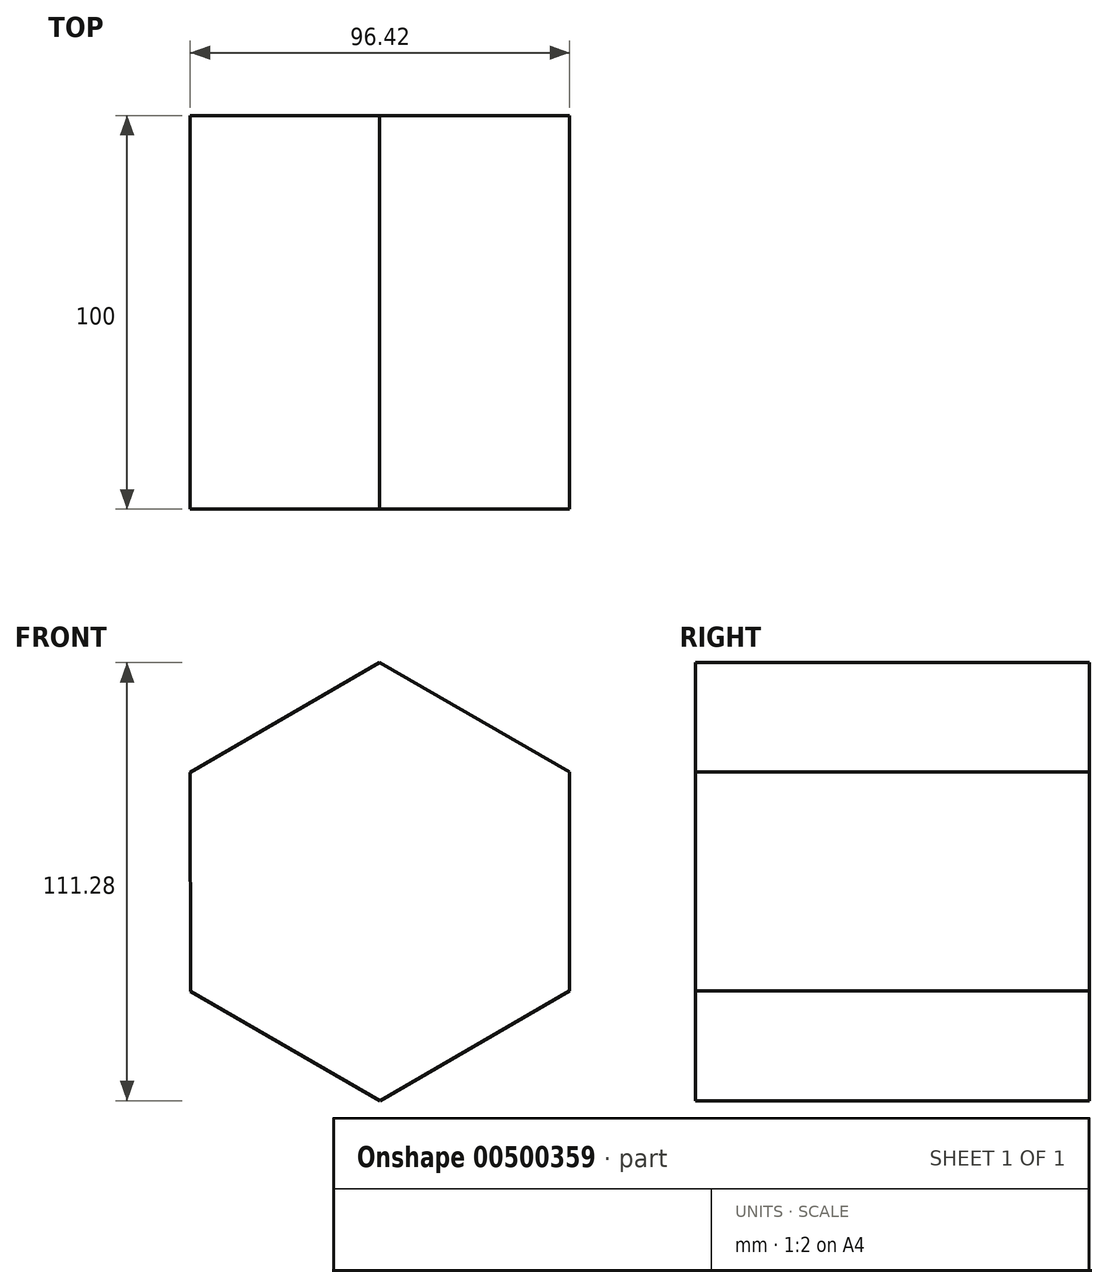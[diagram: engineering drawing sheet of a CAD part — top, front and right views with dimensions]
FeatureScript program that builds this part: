
annotation { "Feature Type Name" : "Feature", "Feature Type Description" : "" }
export const myFeature = defineFeature(function(context is Context, id is Id, definition is map)
    precondition{}
    {
        {
            var Q0;
            Q0=qCreatedBy(makeId("Front.planeOp"),FACE);
            var sketch = newSketch(context, id + "F0", { "sketchPlane" : qUnion([Q0])});
            skCircle(sketch, "E0.cCircle", {"center": v(0, 0) * mm, "radius": 48.18 * mm, "construction": true});
            skLineSegment(sketch, "E0.0", {"start": v(-0.06, 55.64) * mm, "end": v(48.15, 27.87) * mm});
            skLineSegment(sketch, "E0.1", {"start": v(48.15, 27.87) * mm, "end": v(48.21, -27.77) * mm});
            skLineSegment(sketch, "E0.2", {"start": v(48.21, -27.77) * mm, "end": v(0.06, -55.64) * mm});
            skLineSegment(sketch, "E0.3", {"start": v(0.06, -55.64) * mm, "end": v(-48.15, -27.87) * mm});
            skLineSegment(sketch, "E0.4", {"start": v(-48.15, -27.87) * mm, "end": v(-48.21, 27.77) * mm});
            skLineSegment(sketch, "E0.5", {"start": v(-48.21, 27.77) * mm, "end": v(-0.06, 55.64) * mm});
            skPoint(sketch, "E0.0.midPoint", {"position": v(24.05, 41.75) * mm});
            skSolve(sketch);
        }
        {
            var Q0;
            Q0 = qSketchRegion(id + "F0", true);
            extrude(context, id + "F1", {"entities" : qUnion([Q0]), "depth" : 100 * mm});
        }
    });
